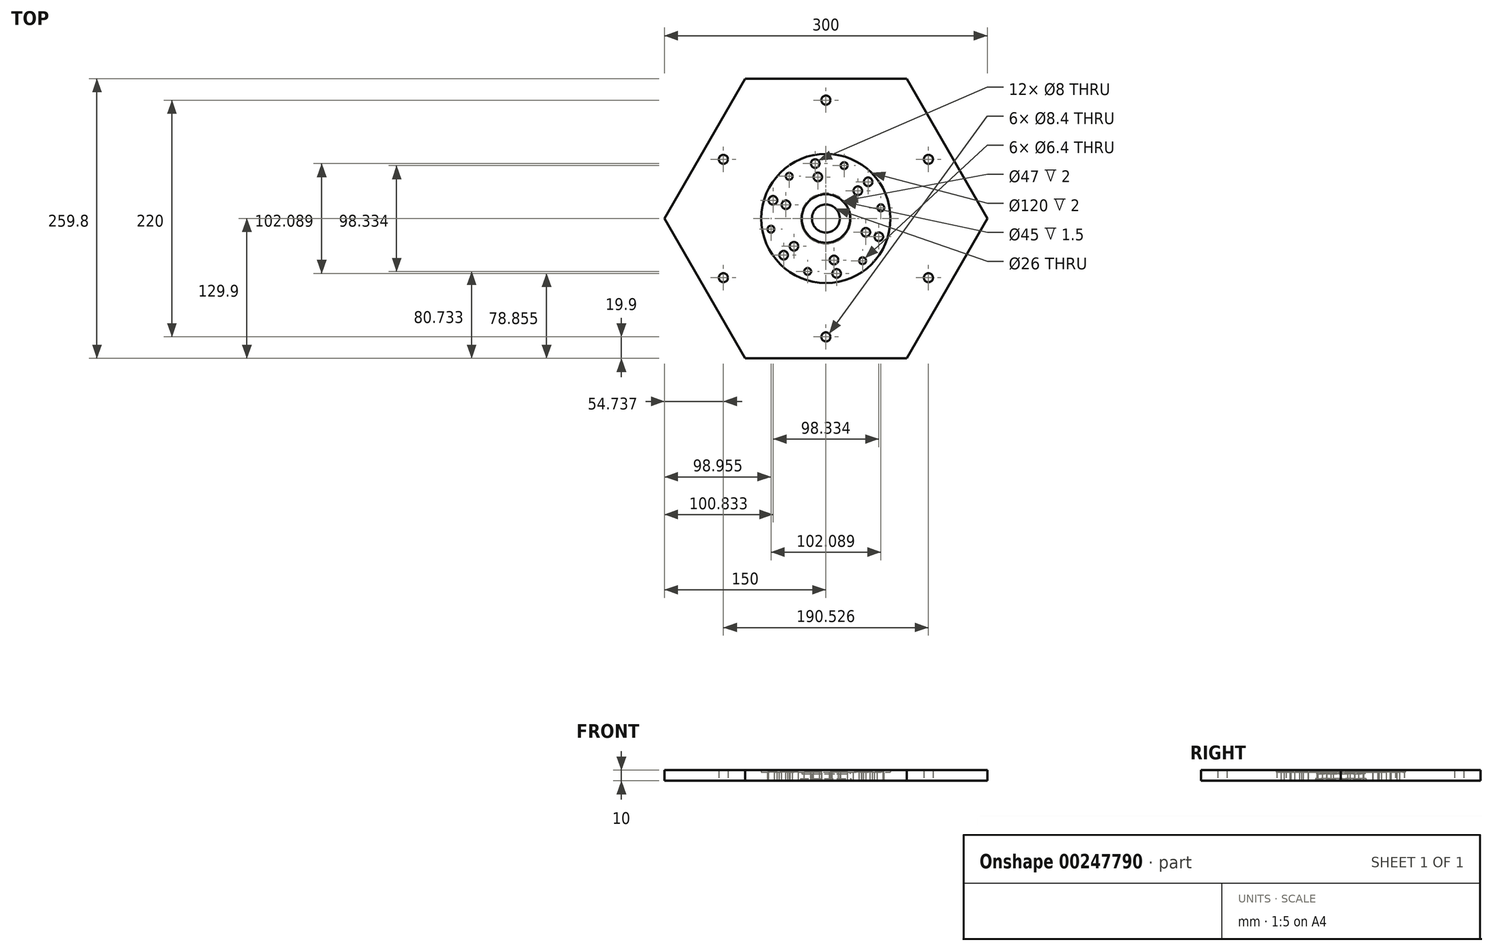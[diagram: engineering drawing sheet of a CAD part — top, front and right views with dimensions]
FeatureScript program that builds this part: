
annotation { "Feature Type Name" : "Feature", "Feature Type Description" : "" }
export const myFeature = defineFeature(function(context is Context, id is Id, definition is map)
    precondition{}
    {
        {
            var Q0;
            Q0=qCreatedBy(makeId("Top.planeOp"),FACE);
            var sketch = newSketch(context, id + "F0", { "sketchPlane" : qUnion([Q0])});
            skCircle(sketch, "E0.cCircle", {"center": v(0, 0) * mm, "radius": 150 * mm, "construction": true});
            skLineSegment(sketch, "E0.0", {"start": v(150, 0) * mm, "end": v(75, -129.9) * mm});
            skLineSegment(sketch, "E0.1", {"start": v(75, -129.9) * mm, "end": v(-75, -129.9) * mm});
            skLineSegment(sketch, "E0.2", {"start": v(-75, -129.9) * mm, "end": v(-150, 0) * mm});
            skLineSegment(sketch, "E0.3", {"start": v(-150, 0) * mm, "end": v(-75, 129.9) * mm});
            skLineSegment(sketch, "E0.4", {"start": v(-75, 129.9) * mm, "end": v(75, 129.9) * mm});
            skLineSegment(sketch, "E0.5", {"start": v(75, 129.9) * mm, "end": v(150, 0) * mm});
            skCircle(sketch, "E1", {"center": v(0, 0) * mm, "radius": 110 * mm, "construction": true});
            skCircle(sketch, "E2", {"center": v(0, 110) * mm, "radius": 4.2 * mm});
            skCircle(sketch, "E3.1.0", {"center": v(-95.26, 55) * mm, "radius": 4.2 * mm});
            skCircle(sketch, "E3.2.0", {"center": v(-95.26, -55) * mm, "radius": 4.2 * mm});
            skCircle(sketch, "E3.3.0", {"center": v(0, -110) * mm, "radius": 4.2 * mm});
            skCircle(sketch, "E3.4.0", {"center": v(95.26, -55) * mm, "radius": 4.2 * mm});
            skCircle(sketch, "E3.5.0", {"center": v(95.26, 55) * mm, "radius": 4.2 * mm});
            skSolve(sketch);
        }
        {
            var Q0;
            Q0=makeQuery(id+"F0.imprint","IMPRINT",FACE,{"disambiguationData":[TD([[makeQuery(id+"F0.imprint","IMPRINT",EDGE,{"derivedFrom":sQuery(id+"F0.wireOp",EDGE,"E0.0")}),-1.0]])]});
            extrude(context, id + "F1", {"entities" : qUnion([Q0]), "depth" : 10 * mm});
        }
        {
            var Q0;
            Q0=qCreatedBy(makeId("Front.planeOp"),FACE);
            var sketch = newSketch(context, id + "F2", { "sketchPlane" : qUnion([Q0])});
            skLineSegment(sketch, "E4", {"start": v(0, 18) * mm, "end": v(0, -22.98) * mm, "construction": true});
            skLineSegment(sketch, "E5", {"start": v(-23.5, 0) * mm, "end": v(8.7, 0) * mm, "construction": true});
            skLineSegment(sketch, "E6", {"start": v(-23.5, -10) * mm, "end": v(0, -10) * mm});
            skLineSegment(sketch, "E7", {"start": v(-60, 18) * mm, "end": v(0, 18) * mm});
            skLineSegment(sketch, "E8", {"start": v(-23.5, 2) * mm, "end": v(-23.5, -10) * mm});
            skLineSegment(sketch, "E9", {"start": v(-23.5, 2) * mm, "end": v(-13, 2) * mm});
            skPoint(sketch, "E10.orphan", {"position": v(-23.5, 0) * mm});
            skLineSegment(sketch, "E11", {"start": v(0, 18) * mm, "end": v(0, -10) * mm});
            skLineSegment(sketch, "E12", {"start": v(-60, 8) * mm, "end": v(-22.5, 8) * mm});
            skLineSegment(sketch, "E13", {"start": v(-60, 18) * mm, "end": v(-60, 8) * mm});
            skLineSegment(sketch, "E14.trimOffspring", {"start": v(-13, 6.5) * mm, "end": v(-13, 2) * mm});
            skLineSegment(sketch, "E15", {"start": v(-13, 6.5) * mm, "end": v(-22.5, 6.5) * mm});
            skLineSegment(sketch, "E16.trimOffspring", {"start": v(-22.5, 8) * mm, "end": v(-22.5, 6.5) * mm});
            skSolve(sketch);
        }
        {
            var Q0;
            Q0=qSketchRegion(id+"F2",true);
            var Q1;
            Q1=sQuery(id+"F2.wireOp",EDGE,"E4");
            revolve(context, id + "F3", {"operationType" : NewBodyOperationType.REMOVE, "entities" : qUnion([Q0]), "axis" : qUnion([Q1]), "revolveType" : RevolveType.FULL, "oppositeDirection" : true});
        }
        {
            var Q0;
            Q0=makeQuery(id+"F3.boolean.opBoolean","COPY",FACE,{"derivedFrom":makeQuery(id+"F3.opRevolve","SWEPT_FACE",FACE,{"disambiguationData":[OSD([sQuery(id+"F2.wireOp",EDGE,"E12")])]})});
            var sketch = newSketch(context, id + "F4", { "sketchPlane" : qUnion([Q0])});
            skLineSegment(sketch, "E17", {"start": v(0.45, -2.3) * mm, "end": v(-8.01, 41.22) * mm, "construction": true});
            skPoint(sketch, "E18", {"position": v(0, 0) * mm});
            skLineSegment(sketch, "E19", {"start": v(2.66, 0.52) * mm, "end": v(-11.37, -2.2) * mm, "construction": true});
            skLineSegment(sketch, "E20", {"start": v(0, 0) * mm, "end": v(46.78, 40.67) * mm, "construction": true});
            skCircle(sketch, "E21", {"center": v(0, 0) * mm, "radius": 21.5 * mm, "construction": true});
            skLineSegment(sketch, "E22.1.1", {"start": v(0, 0) * mm, "end": v(58.6, -20.18) * mm, "construction": true});
            skLineSegment(sketch, "E22.2.1", {"start": v(0, 0) * mm, "end": v(11.83, -60.85) * mm, "construction": true});
            skLineSegment(sketch, "E22.3.1", {"start": v(0, 0) * mm, "end": v(-46.78, -40.67) * mm, "construction": true});
            skLineSegment(sketch, "E22.4.1", {"start": v(0, 0) * mm, "end": v(-58.6, 20.18) * mm, "construction": true});
            skLineSegment(sketch, "E22.5.1", {"start": v(0, 0) * mm, "end": v(-11.83, 60.85) * mm, "construction": true});
            skLineSegment(sketch, "E22.anchor2", {"start": v(0, 0) * mm, "end": v(-11.83, 60.85) * mm, "construction": true});
            skPoint(sketch, "E23", {"position": v(-16.23, -14.1) * mm});
            skCircle(sketch, "E24", {"center": v(0, 0) * mm, "radius": 39.3 * mm, "construction": true});
            skCircle(sketch, "E25", {"center": v(0, 0) * mm, "radius": 52 * mm, "construction": true});
            skPoint(sketch, "E26", {"position": v(-9.92, 51.04) * mm});
            skPoint(sketch, "E27", {"position": v(39.24, 34.12) * mm});
            skPoint(sketch, "E28", {"position": v(49.17, -16.93) * mm});
            skPoint(sketch, "E29", {"position": v(9.92, -51.04) * mm});
            skPoint(sketch, "E30", {"position": v(-39.24, -34.12) * mm});
            skPoint(sketch, "E31", {"position": v(-49.17, 16.93) * mm});
            skPoint(sketch, "E32", {"position": v(-7.5, 38.58) * mm});
            skPoint(sketch, "E33", {"position": v(29.66, 25.78) * mm});
            skPoint(sketch, "E34", {"position": v(37.16, -12.8) * mm});
            skPoint(sketch, "E35", {"position": v(7.5, -38.58) * mm});
            skPoint(sketch, "E36", {"position": v(-29.66, -25.78) * mm});
            skPoint(sketch, "E37", {"position": v(-37.16, 12.8) * mm});
            skLineSegment(sketch, "E38", {"start": v(0, 0) * mm, "end": v(26.77, 77.76) * mm, "construction": true});
            skPoint(sketch, "E39", {"position": v(16.93, 49.17) * mm});
            skPoint(sketch, "E40.1.0", {"position": v(-34.12, 39.24) * mm});
            skPoint(sketch, "E40.2.0", {"position": v(-51.04, -9.92) * mm});
            skPoint(sketch, "E40.3.0", {"position": v(-16.93, -49.17) * mm});
            skPoint(sketch, "E40.4.0", {"position": v(34.12, -39.24) * mm});
            skPoint(sketch, "E40.5.0", {"position": v(51.04, 9.92) * mm});
            skSolve(sketch);
        }
        {
            var Q0;
            Q0=sQuery(id+"F4.wireOp",VERTEX,"E26");
            var Q1;
            Q1=sQuery(id+"F4.wireOp",VERTEX,"E27");
            var Q2;
            Q2=sQuery(id+"F4.wireOp",VERTEX,"E28");
            var Q3;
            Q3=sQuery(id+"F4.wireOp",VERTEX,"E29");
            var Q4;
            Q4=sQuery(id+"F4.wireOp",VERTEX,"E30");
            var Q5;
            Q5=sQuery(id+"F4.wireOp",VERTEX,"E31");
            var Q6;
            Q6=makeQuery(id+"F1.opExtrude","SWEPT_BODY",BODY,{"disambiguationData":[OSD([sQuery(id+"F0.wireOp",EDGE,"E0.0"),sQuery(id+"F0.wireOp",EDGE,"E0.1"),sQuery(id+"F0.wireOp",EDGE,"E0.2"),sQuery(id+"F0.wireOp",EDGE,"E0.3"),sQuery(id+"F0.wireOp",EDGE,"E0.4"),sQuery(id+"F0.wireOp",EDGE,"E0.5")])]});
            hole(context, id + "F5", {"style" : HoleStyle.SIMPLE, "endStyle" : HoleEndStyle.BLIND, "holeDiameter" : 8 * mm, "holeDepth" : 15 * mm, "locations" : qUnion([Q0, Q1, Q2, Q3, Q4, Q5]), "scope" : qUnion([Q6])});
        }
        {
            var Q0;
            Q0=sQuery(id+"F4.wireOp",VERTEX,"E32");
            var Q1;
            Q1=sQuery(id+"F4.wireOp",VERTEX,"E33");
            var Q2;
            Q2=sQuery(id+"F4.wireOp",VERTEX,"E34");
            var Q3;
            Q3=sQuery(id+"F4.wireOp",VERTEX,"E35");
            var Q4;
            Q4=sQuery(id+"F4.wireOp",VERTEX,"E36");
            var Q5;
            Q5=sQuery(id+"F4.wireOp",VERTEX,"E37");
            var Q6;
            Q6=makeQuery(id+"F1.opExtrude","SWEPT_BODY",BODY,{"disambiguationData":[OSD([sQuery(id+"F0.wireOp",EDGE,"E0.0"),sQuery(id+"F0.wireOp",EDGE,"E0.1"),sQuery(id+"F0.wireOp",EDGE,"E0.2"),sQuery(id+"F0.wireOp",EDGE,"E0.3"),sQuery(id+"F0.wireOp",EDGE,"E0.4"),sQuery(id+"F0.wireOp",EDGE,"E0.5")])]});
            hole(context, id + "F6", {"style" : HoleStyle.SIMPLE, "endStyle" : HoleEndStyle.BLIND, "holeDiameter" : 8 * mm, "holeDepth" : 15 * mm, "locations" : qUnion([Q0, Q1, Q2, Q3, Q4, Q5]), "scope" : qUnion([Q6])});
        }
        {
            var Q0;
            Q0=sQuery(id+"F4.wireOp",VERTEX,"E40.1.0");
            var Q1;
            Q1=sQuery(id+"F4.wireOp",VERTEX,"E39");
            var Q2;
            Q2=sQuery(id+"F4.wireOp",VERTEX,"E40.5.0");
            var Q3;
            Q3=sQuery(id+"F4.wireOp",VERTEX,"E40.4.0");
            var Q4;
            Q4=sQuery(id+"F4.wireOp",VERTEX,"E40.3.0");
            var Q5;
            Q5=sQuery(id+"F4.wireOp",VERTEX,"E40.2.0");
            var Q6;
            Q6=makeQuery(id+"F1.opExtrude","SWEPT_BODY",BODY,{"disambiguationData":[OSD([sQuery(id+"F0.wireOp",EDGE,"E0.0"),sQuery(id+"F0.wireOp",EDGE,"E0.1"),sQuery(id+"F0.wireOp",EDGE,"E0.2"),sQuery(id+"F0.wireOp",EDGE,"E0.3"),sQuery(id+"F0.wireOp",EDGE,"E0.4"),sQuery(id+"F0.wireOp",EDGE,"E0.5"),sQuery(id+"F0.wireOp",EDGE,"E2"),sQuery(id+"F0.wireOp",EDGE,"E3.1.0"),sQuery(id+"F0.wireOp",EDGE,"E3.2.0"),sQuery(id+"F0.wireOp",EDGE,"E3.3.0"),sQuery(id+"F0.wireOp",EDGE,"E3.4.0"),sQuery(id+"F0.wireOp",EDGE,"E3.5.0")])]});
            hole(context, id + "F7", {"style" : HoleStyle.SIMPLE, "endStyle" : HoleEndStyle.BLIND, "holeDiameter" : 6.4 * mm, "holeDepth" : 20 * mm, "locations" : qUnion([Q0, Q1, Q2, Q3, Q4, Q5]), "scope" : qUnion([Q6])});
        }
    });
